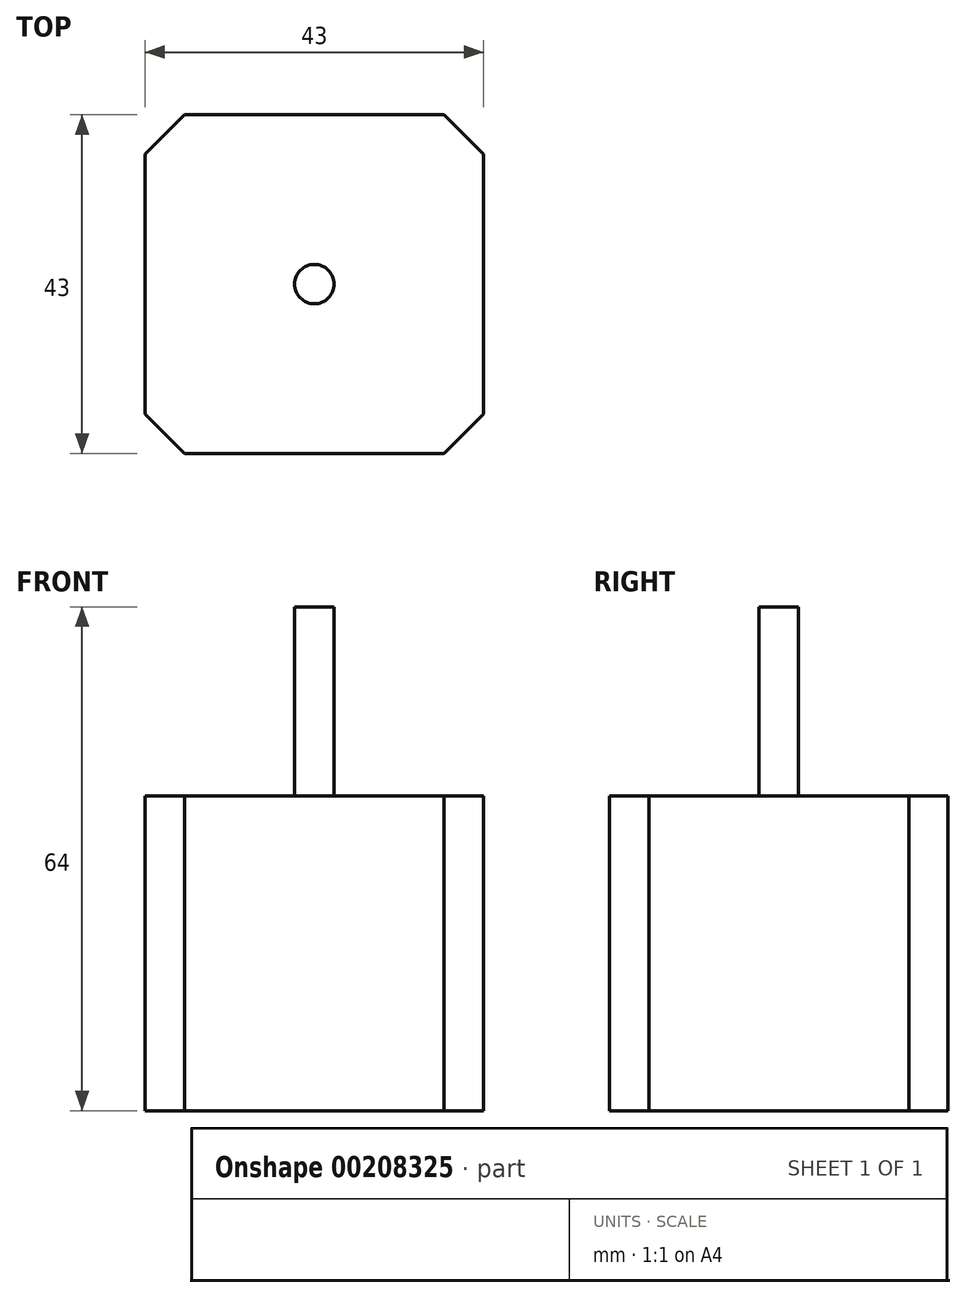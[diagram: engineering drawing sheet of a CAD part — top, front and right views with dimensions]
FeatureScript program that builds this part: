
annotation { "Feature Type Name" : "Feature", "Feature Type Description" : "" }
export const myFeature = defineFeature(function(context is Context, id is Id, definition is map)
    precondition{}
    {
        {
            var Q0;
            Q0=qCreatedBy(makeId("Top.planeOp"),FACE);
            var sketch = newSketch(context, id + "F0", { "sketchPlane" : qUnion([Q0])});
            skLineSegment(sketch, "E0.bottom", {"start": v(21.5, 21.5) * mm, "end": v(-21.5, 21.5) * mm});
            skLineSegment(sketch, "E0.top", {"start": v(21.5, -21.5) * mm, "end": v(-21.5, -21.5) * mm});
            skLineSegment(sketch, "E0.left", {"start": v(21.5, 21.5) * mm, "end": v(21.5, -21.5) * mm});
            skLineSegment(sketch, "E0.right", {"start": v(-21.5, 21.5) * mm, "end": v(-21.5, -21.5) * mm});
            skPoint(sketch, "E0.middle", {"position": v(0, 0) * mm});
            skSolve(sketch);
        }
        {
            var Q0;
            Q0=qSketchRegion(id+"F0",true);
            extrude(context, id + "F1", {"entities" : qUnion([Q0]), "depth" : 40 * mm});
        }
        {
            var Q0;
            Q0=makeQuery(id+"F1.opExtrude","CAP_FACE",FACE,{"disambiguationData":[OSD([sQuery(id+"F0.wireOp",EDGE,"E0.bottom"),sQuery(id+"F0.wireOp",EDGE,"E0.top"),sQuery(id+"F0.wireOp",EDGE,"E0.left"),sQuery(id+"F0.wireOp",EDGE,"E0.right")])],"isStart":false});
            var sketch = newSketch(context, id + "F2", { "sketchPlane" : qUnion([Q0])});
            skCircle(sketch, "E1", {"center": v(0, 0) * mm, "radius": 2.5 * mm});
            skSolve(sketch);
        }
        {
            var Q0;
            Q0=qSketchRegion(id+"F2",true);
            extrude(context, id + "F3", {"entities" : qUnion([Q0]), "operationType" : NewBodyOperationType.ADD, "depth" : 24 * mm});
        }
        {
            var Q0;
            Q0=makeQuery(id+"F1.opExtrude","SWEPT_EDGE",EDGE,{"disambiguationData":[OSD([sQuery(id+"F0.wireOp",EDGE,"E0.top"),sQuery(id+"F0.wireOp",EDGE,"E0.right")])]});
            var Q1;
            Q1=makeQuery(id+"F1.opExtrude","SWEPT_EDGE",EDGE,{"disambiguationData":[OSD([sQuery(id+"F0.wireOp",EDGE,"E0.top"),sQuery(id+"F0.wireOp",EDGE,"E0.left")])]});
            var Q2;
            Q2=makeQuery(id+"F1.opExtrude","SWEPT_EDGE",EDGE,{"disambiguationData":[OSD([sQuery(id+"F0.wireOp",EDGE,"E0.bottom"),sQuery(id+"F0.wireOp",EDGE,"E0.left")])]});
            var Q3;
            Q3=makeQuery(id+"F1.opExtrude","SWEPT_EDGE",EDGE,{"disambiguationData":[OSD([sQuery(id+"F0.wireOp",EDGE,"E0.bottom"),sQuery(id+"F0.wireOp",EDGE,"E0.right")])]});
            chamfer(context, id + "F4", {"entities" : qUnion([Q0, Q1, Q2, Q3]), "width" : 5 * mm, "tangentPropagation" : true});
        }
    });
